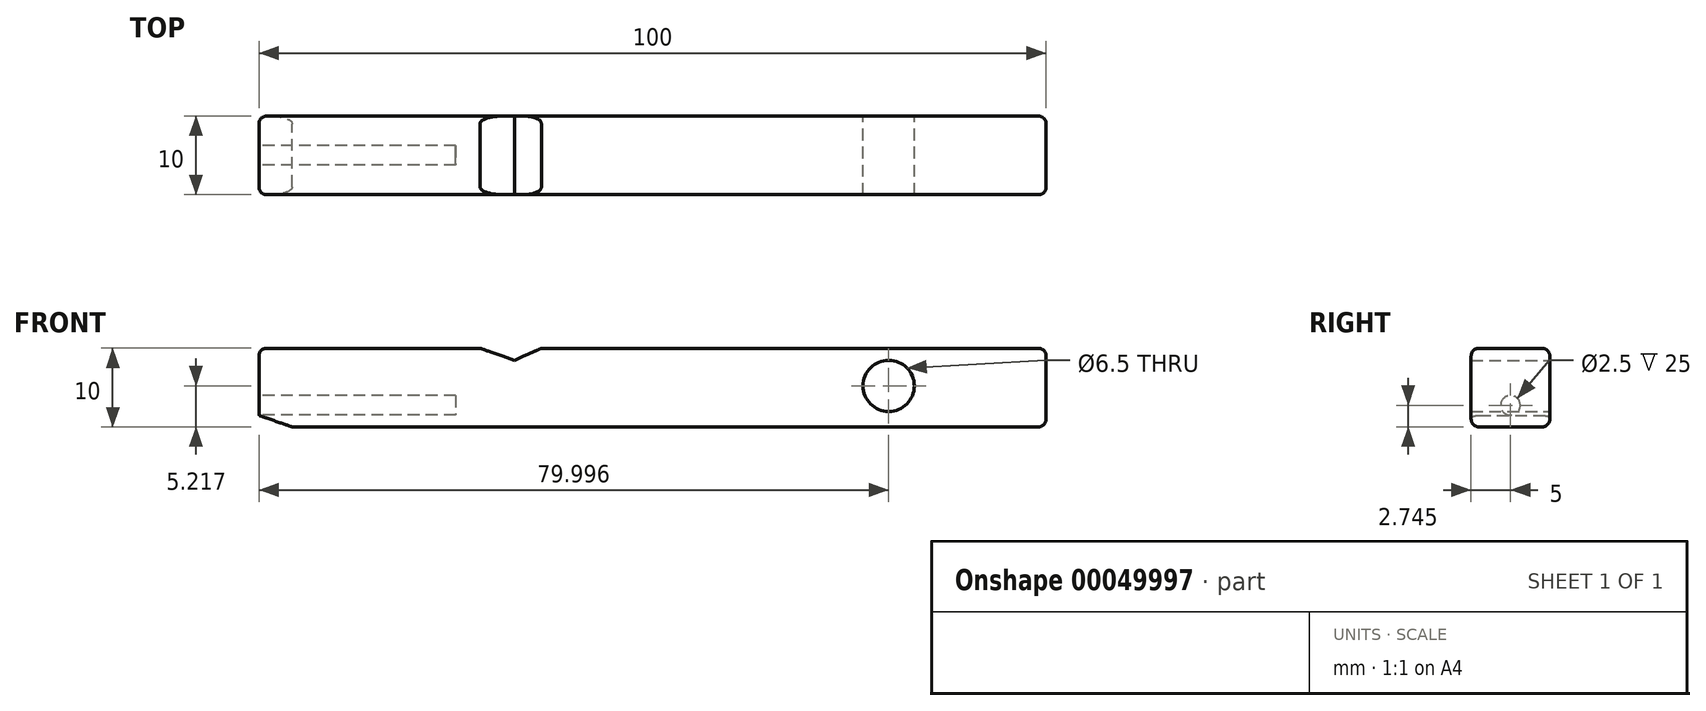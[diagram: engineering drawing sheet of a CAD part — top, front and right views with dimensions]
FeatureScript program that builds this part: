
annotation { "Feature Type Name" : "Feature", "Feature Type Description" : "" }
export const myFeature = defineFeature(function(context is Context, id is Id, definition is map)
    precondition{}
    {
        {
            var Q0;
            Q0=qCreatedBy(makeId("Front.planeOp"),FACE);
            var sketch = newSketch(context, id + "F0", { "sketchPlane" : qUnion([Q0])});
            skLineSegment(sketch, "E0", {"start": v(-36.37, 14.79) * mm, "end": v(59.4, 14.79) * mm});
            skLineSegment(sketch, "E1", {"start": v(59.4, 14.79) * mm, "end": v(59.4, 24.79) * mm});
            skLineSegment(sketch, "E2", {"start": v(59.4, 24.79) * mm, "end": v(-4.72, 24.79) * mm});
            skLineSegment(sketch, "E3", {"start": v(-40.6, 24.79) * mm, "end": v(-40.6, 14.79) * mm});
            skCircle(sketch, "E4", {"center": v(39.4, 20) * mm, "radius": 3.25 * mm});
            skLineSegment(sketch, "E5", {"start": v(-12.52, 24.79) * mm, "end": v(-8.14, 23.25) * mm});
            skLineSegment(sketch, "E6", {"start": v(-8.14, 23.25) * mm, "end": v(-4.72, 24.79) * mm});
            skLineSegment(sketch, "E7.trimOffspring", {"start": v(-12.52, 24.79) * mm, "end": v(-40.6, 24.79) * mm});
            skLineSegment(sketch, "E8", {"start": v(-36.37, 14.79) * mm, "end": v(-40.6, 16.25) * mm});
            skSolve(sketch);
        }
        {
            var Q0;
            Q0 = qSketchRegion(id + "F0", true);
            extrude(context, id + "F1", {"entities" : qUnion([Q0]), "depth" : 10 * mm});
        }
        {
            var Q0;
            Q0=makeQuery(id+"F1.opExtrude","SWEPT_FACE",FACE,{"disambiguationData":[OSD([sQuery(id+"F0.wireOp",EDGE,"E3")])]});
            var sketch = newSketch(context, id + "F2", { "sketchPlane" : qUnion([Q0])});
            skCircle(sketch, "E9", {"center": v(5, 17.54) * mm, "radius": 1.25 * mm});
            skPoint(sketch, "E9.centerSnap0", {"position": v(5, 24.79) * mm});
            skSolve(sketch);
        }
        {
            var Q0;
            Q0=makeQuery(id+"F2.imprint","IMPRINT",FACE,{"disambiguationData":[TD([[makeQuery(id+"F2.imprint","IMPRINT",EDGE,{"derivedFrom":sQuery(id+"F2.wireOp",EDGE,"E9")}),1.0]])]});
            extrude(context, id + "F3", {"entities" : qUnion([Q0]), "operationType" : NewBodyOperationType.REMOVE, "oppositeDirection" : true, "depth" : 25 * mm});
        }
        {
            var Q0;
            Q0=makeQuery(id+"F1.opExtrude","CAP_EDGE",EDGE,{"disambiguationData":[OSD([sQuery(id+"F0.wireOp",EDGE,"E7.trimOffspring")])],"isStart":false});
            var Q1;
            Q1=makeQuery(id+"F1.opExtrude","CAP_EDGE",EDGE,{"disambiguationData":[OSD([sQuery(id+"F0.wireOp",EDGE,"E2")])],"isStart":false});
            var Q2;
            Q2=makeQuery(id+"F1.opExtrude","CAP_EDGE",EDGE,{"disambiguationData":[OSD([sQuery(id+"F0.wireOp",EDGE,"E2")])],"isStart":true});
            var Q3;
            Q3=makeQuery(id+"F1.opExtrude","CAP_EDGE",EDGE,{"disambiguationData":[OSD([sQuery(id+"F0.wireOp",EDGE,"E7.trimOffspring")])],"isStart":true});
            var Q4;
            Q4=makeQuery(id+"F1.opExtrude","CAP_EDGE",EDGE,{"disambiguationData":[OSD([sQuery(id+"F0.wireOp",EDGE,"E3")])],"isStart":true});
            var Q5;
            Q5=makeQuery(id+"F1.opExtrude","SWEPT_EDGE",EDGE,{"disambiguationData":[OSD([sQuery(id+"F0.wireOp",EDGE,"E3"),sQuery(id+"F0.wireOp",EDGE,"E7.trimOffspring")])]});
            var Q6;
            Q6=makeQuery(id+"F1.opExtrude","CAP_EDGE",EDGE,{"disambiguationData":[OSD([sQuery(id+"F0.wireOp",EDGE,"E3")])],"isStart":false});
            fillet(context, id + "F4", {"entities" : qUnion([Q0, Q1, Q2, Q3, Q4, Q5, Q6]), "radius" : 1 * mm, "tangentPropagation" : true, "allowEdgeOverflow" : false});
        }
        {
            var Q0;
            Q0=makeQuery(id+"F1.opExtrude","CAP_EDGE",EDGE,{"disambiguationData":[OSD([sQuery(id+"F0.wireOp",EDGE,"E0")])],"isStart":false});
            var Q1;
            Q1=makeQuery(id+"F1.opExtrude","CAP_EDGE",EDGE,{"disambiguationData":[OSD([sQuery(id+"F0.wireOp",EDGE,"E0")])],"isStart":true});
            var Q2;
            Q2=makeQuery(id+"F1.opExtrude","SWEPT_FACE",FACE,{"disambiguationData":[OSD([sQuery(id+"F0.wireOp",EDGE,"E1")])]});
            fillet(context, id + "F5", {"entities" : qUnion([Q0, Q1, Q2]), "radius" : 1 * mm, "tangentPropagation" : true, "allowEdgeOverflow" : false});
        }
    });
